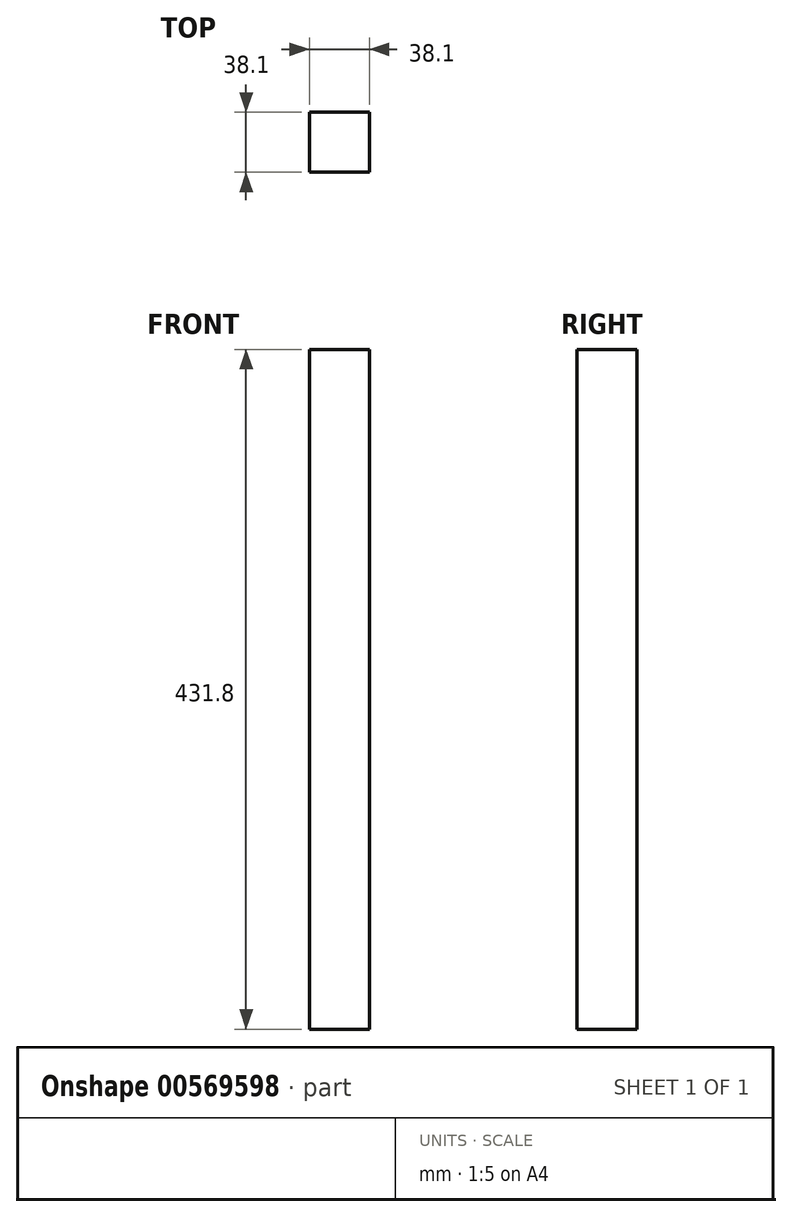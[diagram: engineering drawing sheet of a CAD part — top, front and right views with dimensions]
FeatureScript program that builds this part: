
annotation { "Feature Type Name" : "Feature", "Feature Type Description" : "" }
export const myFeature = defineFeature(function(context is Context, id is Id, definition is map)
    precondition{}
    {
        {
            var Q0;
            Q0=qCreatedBy(makeId("Top.planeOp"),FACE);
            var sketch = newSketch(context, id + "F0", { "sketchPlane" : qUnion([Q0])});
            skLineSegment(sketch, "E0.bottom", {"start": v(19.05, -19.05) * mm, "end": v(-19.05, -19.05) * mm});
            skLineSegment(sketch, "E0.top", {"start": v(19.05, 19.05) * mm, "end": v(-19.05, 19.05) * mm});
            skLineSegment(sketch, "E0.left", {"start": v(19.05, -19.05) * mm, "end": v(19.05, 19.05) * mm});
            skLineSegment(sketch, "E0.right", {"start": v(-19.05, -19.05) * mm, "end": v(-19.05, 19.05) * mm});
            skPoint(sketch, "E0.middle", {"position": v(0, 0) * mm});
            skSolve(sketch);
        }
        {
            var Q0;
            Q0 = qSketchRegion(id + "F0", true);
            extrude(context, id + "F1", {"entities" : qUnion([Q0]), "depth" : 431.8 * mm, "offsetDistance" : 25.4 * mm});
        }
    });
